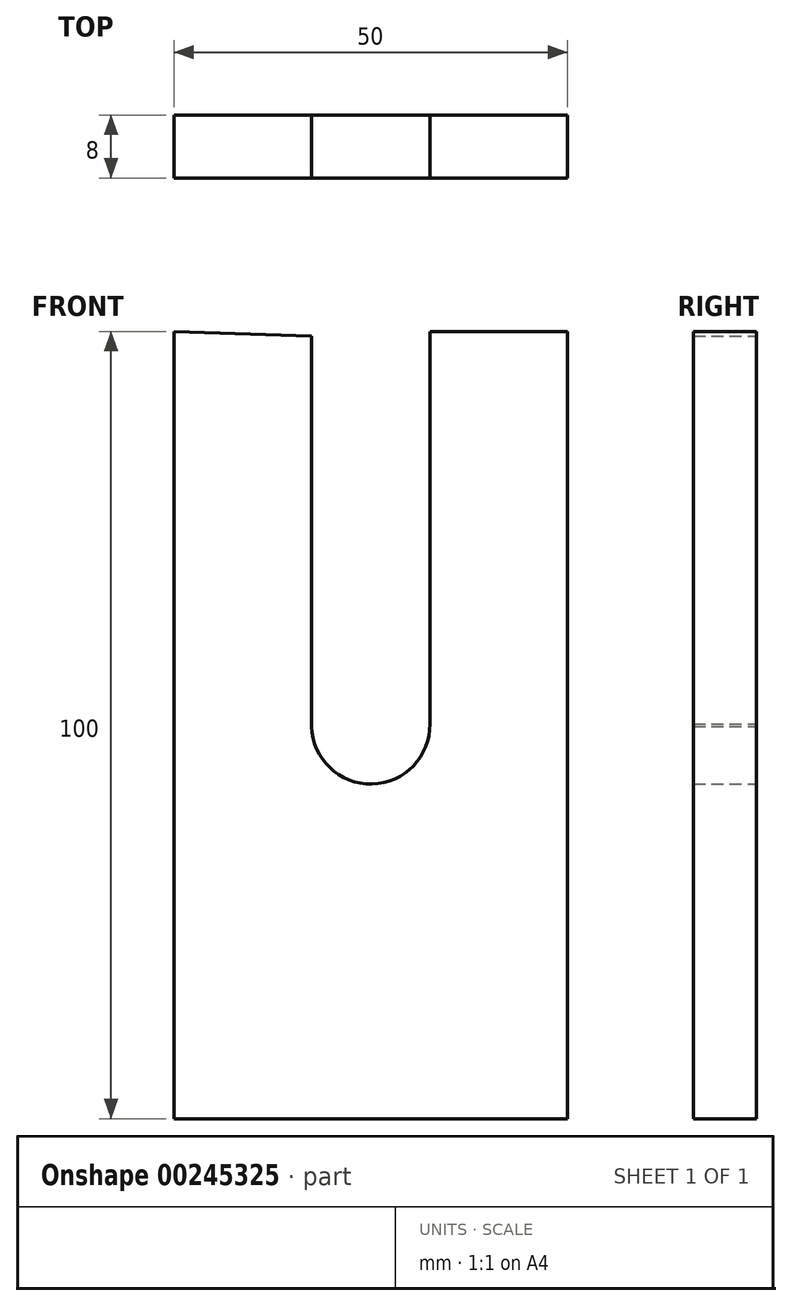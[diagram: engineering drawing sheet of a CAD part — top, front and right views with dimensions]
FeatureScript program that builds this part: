
annotation { "Feature Type Name" : "Feature", "Feature Type Description" : "" }
export const myFeature = defineFeature(function(context is Context, id is Id, definition is map)
    precondition{}
    {
        {
            var Q0;
            Q0=qCreatedBy(makeId("Front.planeOp"),FACE);
            var sketch = newSketch(context, id + "F0", { "sketchPlane" : qUnion([Q0])});
            skLineSegment(sketch, "E0.bottom", {"start": v(0, 0) * mm, "end": v(50, 0) * mm});
            skLineSegment(sketch, "E0.left", {"start": v(0, 0) * mm, "end": v(0, 100) * mm});
            skLineSegment(sketch, "E0.right", {"start": v(50, 0) * mm, "end": v(50, 100) * mm});
            skLineSegment(sketch, "E1", {"start": v(25, 2.35) * mm, "end": v(25, 100) * mm, "construction": true});
            skPoint(sketch, "E1.startSnap0", {"position": v(25, 100) * mm});
            skLineSegment(sketch, "E2.left", {"start": v(32.5, 50.15) * mm, "end": v(32.5, 100) * mm});
            skLineSegment(sketch, "E2.right", {"start": v(17.5, 49.85) * mm, "end": v(17.5, 99.4) * mm});
            skArc(sketch, "E3", {"start": v(17.5, 49.85) * mm, "mid": v(25.15, 42.5) * mm, "end": v(32.5, 50.15) * mm});
            skLineSegment(sketch, "E4.trimOffspring", {"start": v(32.5, 100) * mm, "end": v(50, 100) * mm});
            skPoint(sketch, "E2.top.end.orphan", {"position": v(17.5, 149.85) * mm});
            skPoint(sketch, "E2.top.start.orphan", {"position": v(32.5, 150.15) * mm});
            skLineSegment(sketch, "E5", {"start": v(0, 100) * mm, "end": v(17.5, 99.4) * mm});
            skSolve(sketch);
        }
        {
            var Q0;
            Q0=makeQuery(id+"F0.imprint","IMPRINT",FACE,{"disambiguationData":[TD([[makeQuery(id+"F0.imprint","IMPRINT",EDGE,{"derivedFrom":sQuery(id+"F0.wireOp",EDGE,"E0.bottom")}),1.0]])]});
            extrude(context, id + "F1", {"entities" : qUnion([Q0]), "depth" : 8 * mm});
        }
    });
